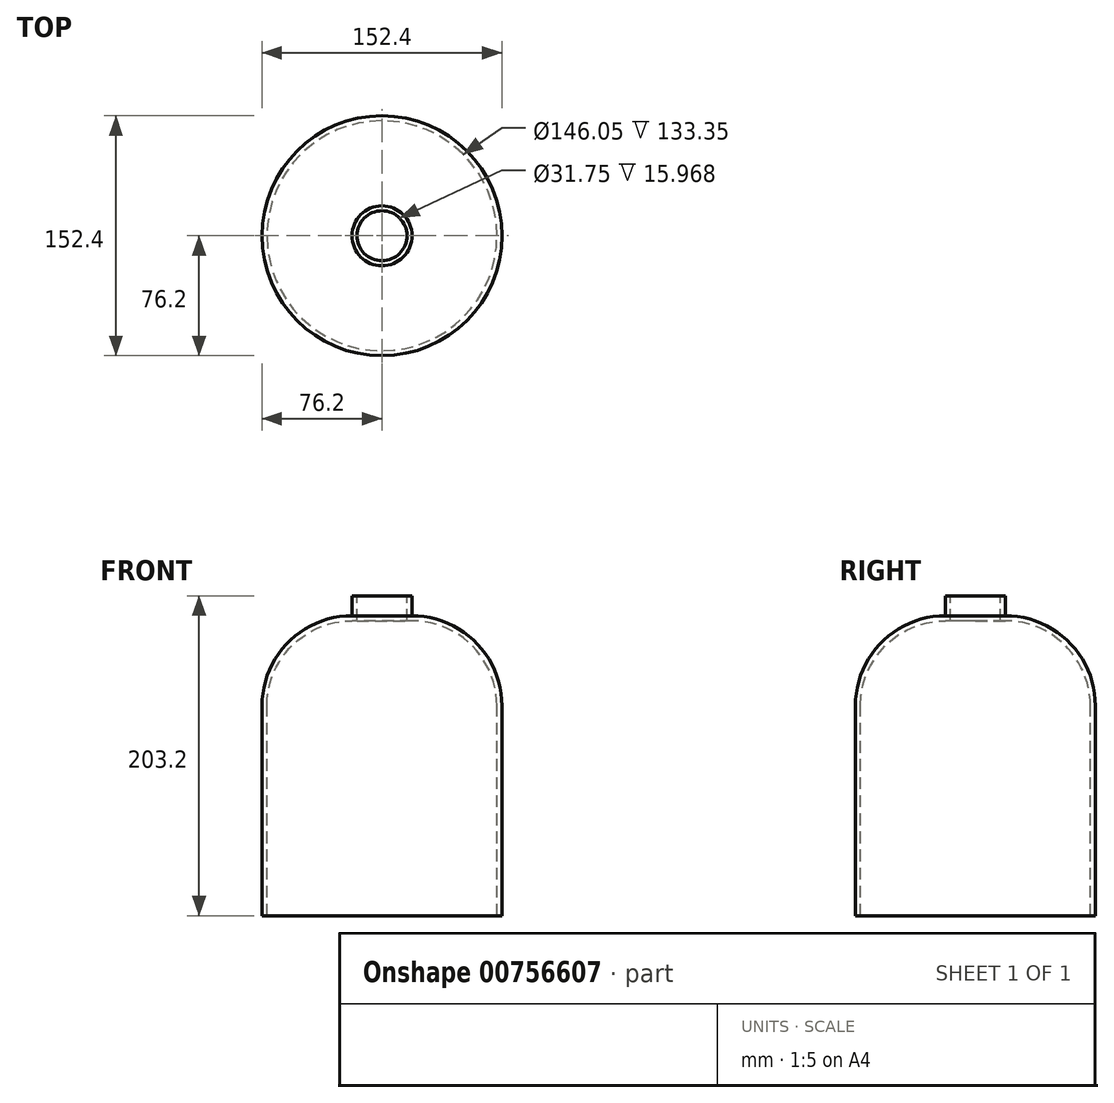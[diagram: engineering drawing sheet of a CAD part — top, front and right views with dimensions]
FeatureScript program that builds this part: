
annotation { "Feature Type Name" : "Feature", "Feature Type Description" : "" }
export const myFeature = defineFeature(function(context is Context, id is Id, definition is map)
    precondition{}
    {
        {
            var Q0;
            Q0=qCreatedBy(makeId("Front.planeOp"),FACE);
            var sketch = newSketch(context, id + "F0", { "sketchPlane" : qUnion([Q0])});
            skLineSegment(sketch, "E0", {"start": v(0, 0) * mm, "end": v(0, -203.2) * mm});
            skLineSegment(sketch, "E1", {"start": v(0, -203.2) * mm, "end": v(76.2, -203.2) * mm});
            skLineSegment(sketch, "E2", {"start": v(76.2, -203.2) * mm, "end": v(76.2, -69.85) * mm});
            skLineSegment(sketch, "E3", {"start": v(0, 0) * mm, "end": v(19.05, 0) * mm});
            skLineSegment(sketch, "E4", {"start": v(19.05, 0) * mm, "end": v(19.05, -12.7) * mm});
            skArc(sketch, "E5", {"start": v(76.2, -69.85) * mm, "mid": v(59.46, -29.44) * mm, "end": v(19.05, -12.7) * mm});
            skSolve(sketch);
        }
        {
            var Q0;
            Q0=makeQuery(id+"F0.imprint","IMPRINT",FACE,{"disambiguationData":[TD([[makeQuery(id+"F0.imprint","IMPRINT",EDGE,{"derivedFrom":sQuery(id+"F0.wireOp",EDGE,"E0")}),1.0]])]});
            var Q1;
            Q1=sQuery(id+"F0.wireOp",EDGE,"E0");
            revolve(context, id + "F1", {"entities" : qUnion([Q0]), "axis" : qUnion([Q1]), "revolveType" : RevolveType.FULL});
        }
        {
            var Q0;
            Q0=makeQuery(id+"F1.opRevolve","SWEPT_FACE",FACE,{"disambiguationData":[OSD([sQuery(id+"F0.wireOp",EDGE,"E1")])]});
            var Q1;
            Q1=makeQuery(id+"F1.opRevolve","SWEPT_FACE",FACE,{"disambiguationData":[OSD([sQuery(id+"F0.wireOp",EDGE,"E3")])]});
            shell(context, id + "F2", {"entities" : qUnion([Q0, Q1]), "thickness" : 3.17 * mm});
        }
    });
